# Revit family: Storage_Shelving-HangSafe_Hooks-Rack
name_source: partatom
category: Specialty Equipment
units: mm (PartAtom-declared; Revit-internal decimal feet)

## family parameters
Classification Number = 23.40.20.27
Cut with Voids When Loaded = No
Enable Cutting in Views = No
Host = Face
Maintain Annotation Orientation = No
Part Type = Normal
Room Calculation Point = No
Round Connector Dimension = Use Diameter
Shared = No

## types (1)
- HangSafe Rack
    Default Elevation = 4' - 0"
    Depth = 0' - 2"
    Description = HangSafe Hooks Rack System
    Finish = Solid Oak - HangSafe Hooks - Cherry Stain
    Hardware Finish = Metal - HangSafe Hooks - Stainless Steel
    Height = 0' - 7"
    Hook Finish = Plastic - HangSafe Hooks - Polycarbonate
    Manufacturer = HangSafe Hooks
    Manufacturer Fax Number = (417)-725-8901
    Model = Rack
    Product Documentation Link = http://hangsafehooks.com
    Product Name = HangSafe Rack
    URL = http://hangsafehooks.com

## geometry (parser evidence)
native form markers: Sweep x4
no freeform markers — native parametric forms only
